# Revit family: Acionador Alarme AMPW ILUMAC
name_source: partatom
category: Dispositivos de alarme de incêndio
units: mm (PartAtom-declared; Revit-internal decimal feet)

## family parameters
Com base no plano de trabalho = Não
Compartilhado = Não
Corte com vazios quando carregada = Não
Cota do conector redondo = Utilizar diâmetro
Manter orientação da anotação = Não
Número OmniClass = 23.80.30.11.17
Ponto de cálculo do ambiente = Não
Sempre na vertical = Sim
Tipo de parte = Normal
Título OmniClass = Distribution Boards and Control Panels

## types (2) — shared parameters
Código do Produto = 02039
Dimensões (AxLxP) = 144x122x70mm
Fabricante = ILUMAC
Fixação = Sobrepor com furação para rosca 3/4” BSP
Grau de proteção = IP66 (uso externo)
Material da caixa = Alumínio com pintura eletrostática vermelha
Normas técnicas aplicáveis = NBR 17240
Temperatura de operação = -5 à +60oC
Tipo de acionamento = Quebra do vidro
zero-valued in all types: Elevação padrão

## per-type parameters (varying)
| type | Corrente máxima saída para sirenes | Correntes de consumo | Descrição | Endereços programáveis | Impedância do drive de comunicação | Peso | Protocolo de comunicação | Resistência em alarme | Tensão de acionamento do laço | Tensão de operação | Tensão nominal | Tensão nominal2 | Topologia | Umidade relativa |
| AMPW-C |  | 130uA @ 24Vcc em supervisão (150uA max)
10mA @ 24Vcc em alarme (+/-0,5) | Acionador Manual Convencional IP66 AMPW-C |  |  | 695g |  | 410 ohms | < 5.5Vcc | 10 à 28Vcc | 12 / 24Vcc | 12 / 24Vcc | Classe B (2 fios) | 0 à 85% (sem condensação) |
| AMPW-E | 50mA @ 24Vcc | 400uA @ 24Vcc em supervisão.
3mA @ 24Vcc em alarme

10mA @ 24Vcc em alarme (+/-0,5) | Acionador Manual Endereçável IP66 AMPW-E | 1 à 500 | 47K Ohms | 700g | ALF-500 (proprietário) | Não se aplica | Não se aplica | 22 à 28Vcc | 24Vcc | Não se aplica | Não se aplica | 0 à 95% (sem condensação) |

note: column(s) folded — value = type name in every type: Modelo
